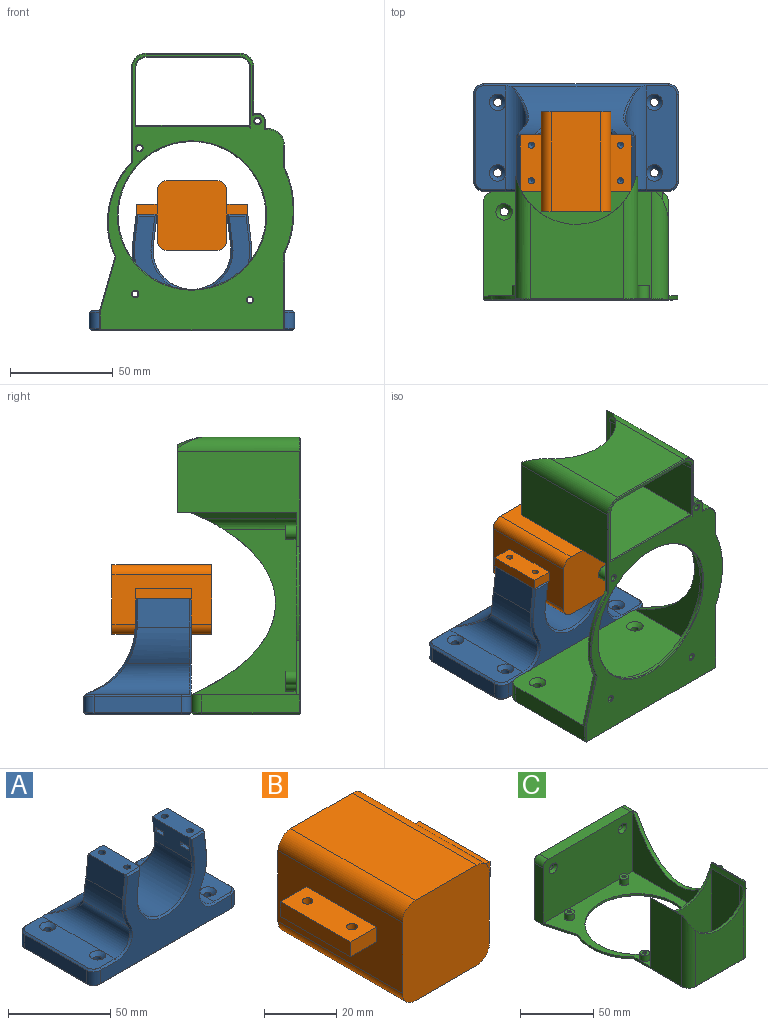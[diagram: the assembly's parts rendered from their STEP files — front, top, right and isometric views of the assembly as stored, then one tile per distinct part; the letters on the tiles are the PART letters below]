
ASSEMBLY  parts=3 mates=2
PART A: 108 faces, bbox 100.2x52.6x56.8 mm
  f0: plane 12.1x9.68mm, normal (0,1,0), area 99.3mm2, adj f52,f96,f98,f99
  f1: plane 50.4x14.86mm, normal (0,0,1), area 641.5mm2, adj f12,f58,f60,f72,f73,f74,f76,f78
  f2: plane 12.1x9.68mm, normal (0,1,0), area 99.3mm2, adj f52,f88,f89,f90
  f3: plane 25.45x15.19mm, normal (-0.99,0,-0.12), area 360.1mm2, adj f15,f16,f24,f25,f26,f27,f31,f32
  f4: plane 25.45x15.19mm, normal (0.99,0,-0.12), area 360.1mm2, adj f16,f18,f37,f38,f40,f41,f44,f46
  f5: plane 90x54.64mm, normal (0,-1,0), area 1919.6mm2, adj f63,f64,f65,f66,f67,f68,f75,f77
  f6: cylinder r=29.14mm len=30.32mm, axis (0,1,0), area 513.8mm2, adj f7,f17,f66,f86
  f7: cylinder r=10mm len=50.4mm, axis (0,1,0), area 862.9mm2, adj f6,f8,f67,f72,f85
  f8: plane 50.4x14.86mm, normal (0,0,1), area 641.5mm2, adj f7,f54,f56,f68,f69,f70,f71,f72
  f9: plane 42.4x8mm, normal (-1,0,0), area 339.2mm2, adj f62,f64,f70,f103
  f10: plane 98x50.4mm, normal (0,0,-1), area 4875.2mm2, adj f53,f55,f57,f59,f100,f101,f102,f103
  f11: plane 42.4x8mm, normal (1,0,0), area 339.2mm2, adj f61,f63,f74,f104
  f12: cylinder r=10mm len=50.4mm, axis (0,1,0), area 862.9mm2, adj f1,f13,f72,f80,f93
  f13: cylinder r=29.14mm len=30.32mm, axis (0,1,0), area 513.8mm2, adj f12,f14,f82,f95
  f14: plane 25.42x13.97mm, normal (0.99,0,0.12), area 357.2mm2, adj f13,f15,f84,f97,f99
  f15: plane 25.4x10.22mm, normal (0,0,1), area 241.4mm2, adj f3,f14,f21,f22,f83,f98
  f16: cylinder r=19mm len=38mm, axis (0,1,0), area 1637.1mm2, adj f3,f4,f79,f92
  f17: plane 25.42x13.97mm, normal (-0.99,0,0.12), area 357.2mm2, adj f6,f18,f65,f87,f88
  f18: plane 25.4x10.22mm, normal (0,0,1), area 241.4mm2, adj f4,f17,f19,f20,f75,f89
  f19: cylinder r=1.7mm len=6mm, axis (0,0,1), area 64.1mm2, adj f18,f48
  f20: cylinder r=1.7mm len=6mm, axis (0,0,1), area 64.1mm2, adj f18,f41
  f21: cylinder r=1.7mm len=6mm, axis (0,0,1), area 64.1mm2, adj f15,f32
  f22: cylinder r=1.7mm len=6mm, axis (0,0,1), area 64.1mm2, adj f15,f25
  f23: plane 5.7x2.5mm, normal (-1,0,0), area 14.2mm2, adj f24,f25,f26,f27
  f24: plane 6.56x5.7mm, normal (0,0,1), area 28.3mm2, adj f3,f23,f26,f27,f29
  f25: plane 6.87x5.7mm, normal (0,0,-1), area 30.1mm2, adj f3,f22,f23,f26,f27
  f26: plane 6.87x2.5mm, normal (0,1,0), area 16.8mm2, adj f3,f23,f24,f25
  f27: plane 6.87x2.5mm, normal (0,-1,0), area 16.8mm2, adj f3,f23,f24,f25
  f28: cone r=0mm half-angle=59deg, axis (0,0,1), area 10.6mm2, adj f29
  f29: cylinder r=1.7mm len=16.5mm, axis (0,0,1), area 176.2mm2, adj f24,f28
  f30: plane 5.7x2.5mm, normal (-1,0,0), area 14.2mm2, adj f31,f32,f33,f34
  f31: plane 6.56x5.7mm, normal (0,0,1), area 28.3mm2, adj f3,f30,f33,f34,f36
  f32: plane 6.87x5.7mm, normal (0,0,-1), area 30.1mm2, adj f3,f21,f30,f33,f34
  f33: plane 6.87x2.5mm, normal (0,-1,0), area 16.8mm2, adj f3,f30,f31,f32
  f34: plane 6.87x2.5mm, normal (0,1,0), area 16.8mm2, adj f3,f30,f31,f32
  f35: cone r=0mm half-angle=59deg, axis (0,0,1), area 10.6mm2, adj f36
  f36: cylinder r=1.7mm len=16.5mm, axis (0,0,1), area 176.2mm2, adj f31,f35
  f37: plane 6.87x2.5mm, normal (0,1,0), area 16.8mm2, adj f4,f39,f40,f41
  f38: plane 6.87x2.5mm, normal (0,-1,0), area 16.8mm2, adj f4,f39,f40,f41
  f39: plane 5.7x2.5mm, normal (1,0,0), area 14.2mm2, adj f37,f38,f40,f41
  f40: plane 6.56x5.7mm, normal (0,0,1), area 28.3mm2, adj f4,f37,f38,f39,f43
  f41: plane 6.87x5.7mm, normal (0,0,-1), area 30.1mm2, adj f4,f20,f37,f38,f39
  f42: cone r=0mm half-angle=59deg, axis (0,0,1), area 10.6mm2, adj f43
  f43: cylinder r=1.7mm len=16.5mm, axis (0,0,1), area 176.2mm2, adj f40,f42
  f44: plane 6.87x2.5mm, normal (0,-1,0), area 16.8mm2, adj f4,f45,f47,f48
  f45: plane 5.7x2.5mm, normal (1,0,0), area 14.2mm2, adj f44,f46,f47,f48
  f46: plane 6.87x2.5mm, normal (0,1,0), area 16.8mm2, adj f4,f45,f47,f48
  f47: plane 6.56x5.7mm, normal (0,0,1), area 28.3mm2, adj f4,f44,f45,f46,f50
  f48: plane 6.87x5.7mm, normal (0,0,-1), area 30.1mm2, adj f4,f19,f44,f45,f46
  f49: cone r=0mm half-angle=59deg, axis (0,0,1), area 10.6mm2, adj f50
  f50: cylinder r=1.7mm len=16.5mm, axis (0,0,1), area 176.2mm2, adj f47,f49
  f51: plane 90x8mm, normal (0,1,0), area 720mm2, adj f61,f62,f72,f107
  f52: cylinder r=35mm len=61.52mm, axis (-1,0,0), area 1413.2mm2, adj f0,f2,f72,f85,f86,f87,f91,f92
  f53: cylinder r=2mm len=8mm, axis (0,0,1), area 100.5mm2, adj f10,f54
  f54: cone r=2mm half-angle=45deg, axis (0,0,1), area 53.3mm2, adj f8,f53
  f55: cylinder r=2mm len=8mm, axis (0,0,1), area 100.5mm2, adj f10,f56
  f56: cone r=2mm half-angle=45deg, axis (0,0,1), area 53.3mm2, adj f8,f55
  f57: cylinder r=2mm len=8mm, axis (0,0,1), area 100.5mm2, adj f10,f58
  f58: cone r=2mm half-angle=45deg, axis (0,0,1), area 53.3mm2, adj f1,f57
  f59: cylinder r=2mm len=8mm, axis (0,0,1), area 100.5mm2, adj f10,f60
  f60: cone r=2mm half-angle=45deg, axis (0,0,1), area 53.3mm2, adj f1,f59
  f61: cylinder r=5mm len=8mm, axis (0,0,-1), area 62.8mm2, adj f11,f51,f73,f106
  f62: cylinder r=5mm len=8mm, axis (0,0,1), area 62.8mm2, adj f9,f51,f71,f105
  f63: cylinder r=5mm len=8mm, axis (0,0,-1), area 62.8mm2, adj f5,f11,f76,f102
  f64: cylinder r=5mm len=8mm, axis (0,0,1), area 62.8mm2, adj f5,f9,f69,f101
  f65: plane 14.08x2.59mm, normal (-0.7,-0.71,0.09), area 19.3mm2, adj f5,f17,f66,f75
  f66: cone r=28.14mm half-angle=45deg, axis (0,1,0), area 25.6mm2, adj f5,f6,f65,f67
  f67: cone r=10mm half-angle=45deg, axis (0,-1,0), area 30.9mm2, adj f5,f7,f66,f68
  f68: plane 10.86x1mm, normal (0,-0.71,0.71), area 15.4mm2, adj f5,f8,f67,f69
  f69: cone r=4mm half-angle=45deg, axis (0,0,-1), area 10mm2, adj f8,f64,f68,f70
  f70: plane 42.4x1mm, normal (-0.71,0,0.71), area 60mm2, adj f8,f9,f69,f71
  f71: cone r=4mm half-angle=45deg, axis (0,0,-1), area 10mm2, adj f8,f62,f70,f72
  f72: plane 90.17x1.65mm, normal (0,0.71,0.71), area 170.4mm2, adj f1,f7,f8,f12,f51,f52,f71,f73
  f73: cone r=4mm half-angle=45deg, axis (0,0,-1), area 10mm2, adj f1,f61,f72,f74
  f74: plane 42.4x1mm, normal (0.71,0,0.71), area 60mm2, adj f1,f11,f73,f76
  f75: plane 10.22x1mm, normal (0,-0.71,0.71), area 13mm2, adj f5,f18,f65,f77
  f76: cone r=4mm half-angle=45deg, axis (0,0,-1), area 10mm2, adj f1,f63,f74,f78
  f77: plane 15.19x2.85mm, normal (0.7,-0.71,-0.09), area 20.8mm2, adj f4,f5,f75,f79
  f78: plane 10.86x1mm, normal (0,-0.71,0.71), area 15.4mm2, adj f1,f5,f76,f80
  f79: cone r=19mm half-angle=45deg, axis (0,-1,0), area 93.4mm2, adj f5,f16,f77,f81
  f80: cone r=10mm half-angle=45deg, axis (0,-1,0), area 30.9mm2, adj f5,f12,f78,f82
  f81: plane 15.19x2.85mm, normal (-0.7,-0.71,-0.09), area 20.8mm2, adj f3,f5,f79,f83
  f82: cone r=28.14mm half-angle=45deg, axis (0,1,0), area 25.6mm2, adj f5,f13,f80,f84
  f83: plane 10.22x1mm, normal (0,-0.71,0.71), area 13mm2, adj f5,f15,f81,f84
  f84: plane 14.08x2.59mm, normal (0.7,-0.71,0.09), area 19.3mm2, adj f5,f14,f82,f83
  f85: bspline ~20.81x15.8mm, area 29.6mm2, adj f7,f52,f72,f86
  f86: bspline ~17.79x5.77mm, area 27.4mm2, adj f6,f52,f85,f87
  f87: bspline ~1.11x1.08mm, area 1.4mm2, adj f17,f52,f86,f88
  f88: plane 13.1x2.47mm, normal (-0.7,0.71,0.09), area 17.9mm2, adj f2,f17,f87,f89
  f89: plane 10.22x1mm, normal (0,0.71,0.71), area 13mm2, adj f2,f18,f88,f90
  f90: plane 13.22x2.61mm, normal (0.7,0.71,-0.09), area 18mm2, adj f2,f4,f89,f91
  f91: bspline ~2.09x1.23mm, area 2.8mm2, adj f4,f52,f90,f92
  f92: bspline ~40.09x21.81mm, area 77.9mm2, adj f16,f52,f91,f94
  f93: bspline ~20.06x15.56mm, area 29.6mm2, adj f12,f52,f72,f95
  f94: bspline ~2.09x1.23mm, area 2.8mm2, adj f3,f52,f92,f96
  f95: bspline ~17.79x5.77mm, area 27.4mm2, adj f13,f52,f93,f97
  f96: plane 13.22x2.61mm, normal (-0.7,0.71,-0.09), area 18mm2, adj f0,f3,f94,f98
  f97: bspline ~1.11x1.08mm, area 1.4mm2, adj f14,f52,f95,f99
  f98: plane 10.22x1mm, normal (0,0.71,0.71), area 13mm2, adj f0,f15,f96,f99
  f99: plane 13.1x2.47mm, normal (0.7,0.71,0.09), area 17.9mm2, adj f0,f14,f97,f98
  f100: plane 90x1mm, normal (0,-0.71,-0.71), area 127.3mm2, adj f5,f10,f101,f102
  f101: cone r=4mm half-angle=45deg, axis (0,0,1), area 10mm2, adj f10,f64,f100,f103
  f102: cone r=4mm half-angle=45deg, axis (0,0,1), area 10mm2, adj f10,f63,f100,f104
  f103: plane 42.4x1mm, normal (-0.71,0,-0.71), area 60mm2, adj f9,f10,f101,f105
  f104: plane 42.4x1mm, normal (0.71,0,-0.71), area 60mm2, adj f10,f11,f102,f106
  f105: cone r=4mm half-angle=45deg, axis (0,0,1), area 10mm2, adj f10,f62,f103,f107
  f106: cone r=4mm half-angle=45deg, axis (0,0,1), area 10mm2, adj f10,f61,f104,f107
  f107: plane 90x1mm, normal (0,0.71,-0.71), area 127.3mm2, adj f10,f51,f105,f106
PART B: 24 faces, bbox 54.4x48.7x34 mm
  f0: plane 48.7x24mm, normal (-1,0,0), area 1031.8mm2, adj f1,f3,f4,f6,f10,f12,f13,f14
  f1: plane 34x34mm, normal (0,-1,0), area 1134.5mm2, adj f0,f2,f3,f4,f5,f7,f8,f9
  f2: plane 48.7x24mm, normal (0,0,1), area 1168.8mm2, adj f1,f3,f6,f8
  f3: cylinder r=5mm len=48.7mm, axis (0,1,0), area 382.5mm2, adj f0,f1,f2,f6
  f4: cylinder r=5mm len=48.7mm, axis (0,1,0), area 382.5mm2, adj f0,f1,f5,f6
  f5: plane 48.7x24mm, normal (0,0,-1), area 1168.8mm2, adj f1,f4,f6,f7
  f6: plane 34x34mm, normal (0,1,0), area 1134.5mm2, adj f0,f2,f3,f4,f5,f7,f8,f9
  f7: cylinder r=5mm len=48.7mm, axis (0,1,0), area 382.5mm2, adj f1,f5,f6,f9
  f8: cylinder r=5mm len=48.7mm, axis (0,1,0), area 382.5mm2, adj f1,f2,f6,f9
  f9: plane 48.7x24mm, normal (1,0,0), area 1031.8mm2, adj f1,f6,f7,f8,f15,f16,f17,f19
  f10: plane 10.22x5mm, normal (0,-1,0), area 51.1mm2, adj f0,f11,f13,f14
  f11: plane 27.4x5mm, normal (-1,0,0), area 137mm2, adj f10,f12,f13,f14
  f12: plane 10.22x5mm, normal (0,1,0), area 51.1mm2, adj f0,f11,f13,f14
  f13: plane 27.4x10.22mm, normal (0,0,-1), area 265.8mm2, adj f0,f10,f11,f12,f22,f23
  f14: plane 27.4x10.22mm, normal (0,0,1), area 265.8mm2, adj f0,f10,f11,f12,f22,f23
  f15: plane 10.22x5mm, normal (0,-1,0), area 51.1mm2, adj f9,f16,f17,f18
  f16: plane 27.4x10.22mm, normal (0,0,1), area 265.8mm2, adj f9,f15,f18,f19,f20,f21
  f17: plane 27.4x10.22mm, normal (0,0,-1), area 265.8mm2, adj f9,f15,f18,f19,f20,f21
  f18: plane 27.4x5mm, normal (1,0,0), area 137mm2, adj f15,f16,f17,f19
  f19: plane 10.22x5mm, normal (0,1,0), area 51.1mm2, adj f9,f16,f17,f18
  f20: cylinder r=1.5mm len=5mm, axis (0,0,-1), area 47.1mm2, adj f16,f17
  f21: cylinder r=1.5mm len=5mm, axis (0,0,-1), area 47.1mm2, adj f16,f17
  f22: cylinder r=1.5mm len=5mm, axis (0,0,-1), area 47.1mm2, adj f13,f14
  f23: cylinder r=1.5mm len=5mm, axis (0,0,-1), area 47.1mm2, adj f13,f14
PART C: 89 faces, bbox 94.9x135.4x60.2 mm
  f0: plane 58x54.97mm, normal (0,1,0), area 2191.9mm2, adj f3,f13,f36,f37,f47
  f1: plane 52.6x6.89mm, normal (0,-1,0), area 325.4mm2, adj f2,f5,f38,f40,f49,f68
  f2: plane 59.6x30.91mm, normal (1,0,0), area 1795.3mm2, adj f1,f9,f11,f28,f35,f40,f62
  f3: plane 88.66x87mm, normal (0,0,1), area 2827.3mm2, adj f0,f4,f7,f13,f16,f17,f27,f39
  f4: plane 86.49x51mm, normal (-1,0,0), area 1659.8mm2, adj f3,f7,f38,f48,f54
  f5: plane 6.6x3.72mm, normal (1,0,0), area 24.6mm2, adj f1,f11,f40,f66
  f6: extruded ~42.24x4.7mm, area 69.8mm2, adj f12,f26,f69
  f7: plane 87x51mm, normal (0,-1,0), area 4330.8mm2, adj f3,f4,f23,f25,f51,f53,f54,f55
  f8: plane 47.28x45.56mm, normal (0,-1,0), area 1800mm2, adj f28,f29,f37,f58
  f9: plane 33.32x0.86mm, normal (0,0,1), area 28mm2, adj f2,f28,f35,f37
  f10: plane 55.81x55.47mm, normal (0,-1,0), area 2298.1mm2, adj f14,f15,f30,f34,f37,f78
  f11: cylinder r=3.82mm len=6.6mm, axis (0,0,-1), area 52.1mm2, adj f2,f5,f40,f64
  f12: plane 42.25x4.71mm, normal (0,0,1), area 134.5mm2, adj f6,f26
  f13: plane 59.6x46.15mm, normal (-1,0,0), area 1801.7mm2, adj f0,f3,f16,f29,f36,f57
  f14: extruded ~1.6x0.57mm, area 1.1mm2, adj f10,f15,f34,f76
  f15: plane 55.81x27.67mm, normal (-1,0,0), area 1521.5mm2, adj f10,f14,f33,f34,f37,f74
  f16: extruded ~45.99x11.86mm, area 79.5mm2, adj f3,f13,f27,f59
  f17: cylinder r=36mm len=72mm, axis (0,0,-1), area 361.9mm2, adj f3,f83
  f18: plane 134.59x94.1mm, normal (0,0,-1), area 4252.3mm2, adj f56,f57,f58,f59,f60,f61,f62,f63
  f19: cylinder r=1.4mm len=6.6mm, axis (0,0,-1), area 58.1mm2, adj f46,f82
  f20: cylinder r=1.4mm len=6.6mm, axis (0,0,-1), area 58.1mm2, adj f40,f81
  f21: cylinder r=1.4mm len=6.6mm, axis (0,0,-1), area 58.1mm2, adj f44,f80
  f22: cylinder r=1.4mm len=6.6mm, axis (0,0,-1), area 58.1mm2, adj f42,f79
  f23: plane 80x8.74mm, normal (0,0,1), area 699.5mm2, adj f7,f54,f55,f86
  f24: plane 88x51.6mm, normal (0,1,0), area 4508.8mm2, adj f50,f52,f65,f84,f85,f86,f87,f88
  f25: plane 47.6x8.74mm, normal (-1,0,0), area 416.2mm2, adj f7,f27,f55,f63,f88
  f26: plane 94.84x52.6mm, normal (1,0,0), area 2131.8mm2, adj f6,f12,f38,f49,f54,f67,f71,f84
  f27: plane 26.31x7.48mm, normal (-0.96,-0.27,0), area 43.8mm2, adj f3,f16,f25,f61
  f28: cylinder r=7mm len=59.6mm, axis (0,0,-1), area 543.6mm2, adj f2,f8,f9,f37,f60
  f29: cylinder r=7mm len=59.6mm, axis (0,0,-1), area 590.9mm2, adj f8,f13,f36,f37,f56
  f30: plane 54x28.19mm, normal (1,0,0), area 1522.3mm2, adj f10,f31,f37,f77
  f31: cylinder r=5mm len=54mm, axis (0,0,-1), area 393.9mm2, adj f30,f32,f37,f75
  f32: plane 47.28x45.56mm, normal (0,1,0), area 1800mm2, adj f31,f33,f37,f73
  f33: cylinder r=5mm len=55.81mm, axis (0,0,-1), area 453.7mm2, adj f15,f32,f37,f72
  f34: plane 0.57x0.43mm, normal (0,0,-1), area 0.1mm2, adj f10,f14,f15
  f35: plane 7x3.42mm, normal (0,1,0), area 13.8mm2, adj f2,f9,f37,f38
  f36: plane 31.09x0.12mm, normal (0,0,1), area 3.7mm2, adj f0,f13,f29,f37
  f37: cylinder r=30mm len=58.48mm, axis (0,-1,0), area 595.4mm2, adj f0,f8,f9,f10,f15,f28,f29,f30
  f38: extruded ~88.47x40.99mm, area 463mm2, adj f1,f4,f26,f35,f37,f39,f47,f48
  f39: plane 44.44x8.39mm, normal (0,1,0), area 373mm2, adj f3,f38,f47,f48
  f40: plane 7.54x5.64mm, normal (0,0,1), area 33mm2, adj f1,f2,f5,f11,f20
  f41: cylinder r=3.4mm len=6.8mm, axis (0,0,-1), area 106.8mm2, adj f3,f42
  f42: plane 6.8x6.8mm, normal (0,0,1), area 30.2mm2, adj f22,f41
  f43: cylinder r=3.4mm len=6.8mm, axis (0,0,-1), area 106.8mm2, adj f3,f44
  f44: plane 6.8x6.8mm, normal (0,0,1), area 30.2mm2, adj f21,f43
  f45: cylinder r=3.4mm len=6.8mm, axis (0,0,-1), area 106.8mm2, adj f3,f46
  f46: plane 6.8x6.8mm, normal (0,0,1), area 30.2mm2, adj f19,f45
  f47: plane 49.91x3.03mm, normal (-0.71,0.71,0), area 201.4mm2, adj f0,f3,f37,f38,f39
  f48: cylinder r=5mm len=44.44mm, axis (0,0,1), area 313.5mm2, adj f3,f4,f38,f39
  f49: cylinder r=8mm len=52.6mm, axis (0,0,1), area 563mm2, adj f1,f26,f38,f70
  f50: cylinder r=2mm len=7.74mm, axis (0,-1,0), area 97.3mm2, adj f24,f51
  f51: cone r=2mm half-angle=45deg, axis (0,-1,0), area 53.3mm2, adj f7,f50
  f52: cylinder r=2mm len=7.74mm, axis (0,-1,0), area 97.3mm2, adj f24,f53
  f53: cone r=2mm half-angle=45deg, axis (0,-1,0), area 53.3mm2, adj f7,f52
  f54: cylinder r=5mm len=11.07mm, axis (0,-1,0), area 75.1mm2, adj f4,f7,f23,f26,f38,f85
  f55: cylinder r=5mm len=8.74mm, axis (0,1,0), area 68.7mm2, adj f7,f23,f25,f87
  f56: cone r=7mm half-angle=45deg, axis (0,0,1), area 6mm2, adj f18,f29,f57,f58
  f57: plane 46.31x0.4mm, normal (-0.71,0,-0.71), area 26.2mm2, adj f13,f18,f56,f59
  f58: plane 45.56x0.4mm, normal (0,-0.71,-0.71), area 25.8mm2, adj f8,f18,f56,f60
  f59: bspline ~50.18x14.08mm, area 28mm2, adj f16,f18,f57,f61
  f60: cone r=7mm half-angle=45deg, axis (0,0,1), area 5.4mm2, adj f18,f28,f58,f62
  f61: plane 26.41x7.91mm, normal (-0.68,-0.19,-0.71), area 15.5mm2, adj f18,f27,f59,f63
  f62: plane 24.63x0.44mm, normal (0.71,0,-0.71), area 13.7mm2, adj f2,f18,f60,f64
  f63: plane 9.14x0.4mm, normal (-0.71,0,-0.71), area 5mm2, adj f18,f25,f61,f88
  f64: cone r=3.82mm half-angle=45deg, axis (0,0,1), area 4.4mm2, adj f11,f18,f62,f66
  f65: plane 88.8x0.4mm, normal (0,0.71,-0.71), area 50mm2, adj f18,f24,f84,f88
  f66: plane 4.12x0.4mm, normal (0.71,0,-0.71), area 2.2mm2, adj f5,f18,f64,f68
  f67: plane 36.81x0.4mm, normal (0.71,0,-0.71), area 20.7mm2, adj f18,f26,f69,f84
  f68: plane 1.65x0.4mm, normal (0,-0.71,-0.71), area 0.8mm2, adj f1,f18,f66,f70
  f69: bspline ~46.27x6.1mm, area 24.6mm2, adj f6,f18,f67,f71
  f70: cone r=7.6mm half-angle=45deg, axis (0,0,1), area 6.9mm2, adj f18,f49,f68,f71
  f71: plane 10.94x0.4mm, normal (0.71,0,-0.71), area 6.2mm2, adj f18,f26,f69,f70
  f72: cone r=5.4mm half-angle=45deg, axis (0,0,-1), area 5.2mm2, adj f18,f33,f73,f74
  f73: plane 45.56x0.4mm, normal (0,0.71,-0.71), area 25.8mm2, adj f18,f32,f72,f75
  f74: plane 28.48x0.4mm, normal (-0.71,0,-0.71), area 15.9mm2, adj f15,f18,f72,f76
  f75: cone r=5.4mm half-angle=45deg, axis (0,0,-1), area 4.6mm2, adj f18,f31,f73,f77
  f76: bspline ~1.45x1.23mm, area 0.6mm2, adj f14,f18,f74,f78
  f77: plane 28.59x0.4mm, normal (0.71,0,-0.71), area 16.1mm2, adj f18,f30,f75,f78
  f78: plane 55.3x0.4mm, normal (0,-0.71,-0.71), area 31.1mm2, adj f10,f18,f76,f77
  f79: cone r=1.4mm half-angle=45deg, axis (0,0,-1), area 5.7mm2, adj f18,f22
  f80: cone r=1.4mm half-angle=45deg, axis (0,0,-1), area 5.7mm2, adj f18,f21
  f81: cone r=1.4mm half-angle=45deg, axis (0,0,-1), area 5.7mm2, adj f18,f20
  f82: cone r=1.4mm half-angle=45deg, axis (0,0,-1), area 5.7mm2, adj f18,f19
  f83: cone r=36.4mm half-angle=45deg, axis (0,0,-1), area 128.7mm2, adj f17,f18
  f84: plane 48x1mm, normal (0.71,0.71,0), area 67.7mm2, adj f18,f24,f26,f65,f67,f85
  f85: cone r=4mm half-angle=45deg, axis (0,-1,0), area 10mm2, adj f24,f54,f84,f86
  f86: plane 80x1mm, normal (0,0.71,0.71), area 113.1mm2, adj f23,f24,f85,f87
  f87: cone r=4mm half-angle=45deg, axis (0,-1,0), area 10mm2, adj f24,f55,f86,f88
  f88: plane 48x1mm, normal (-0.71,0.71,0), area 67.7mm2, adj f18,f24,f25,f63,f65,f87
PLACE A t=(-26.46,-24.73,6.43)mm
PLACE B t=(-26.46,-24.73,6.43)mm
PLACE C rot(axis=(-1,0,0),90deg) t=(-61.74,-91.43,10.41)mm
MATE fastened B.f22 <-> A.f20  axis (0,0,-1) through (-48.21,-33.43,6.93)mm
MATE fastened B.f1 <-> C.f17  axis (0,-1,0) through (-26.46,-48.43,6.43)mm
